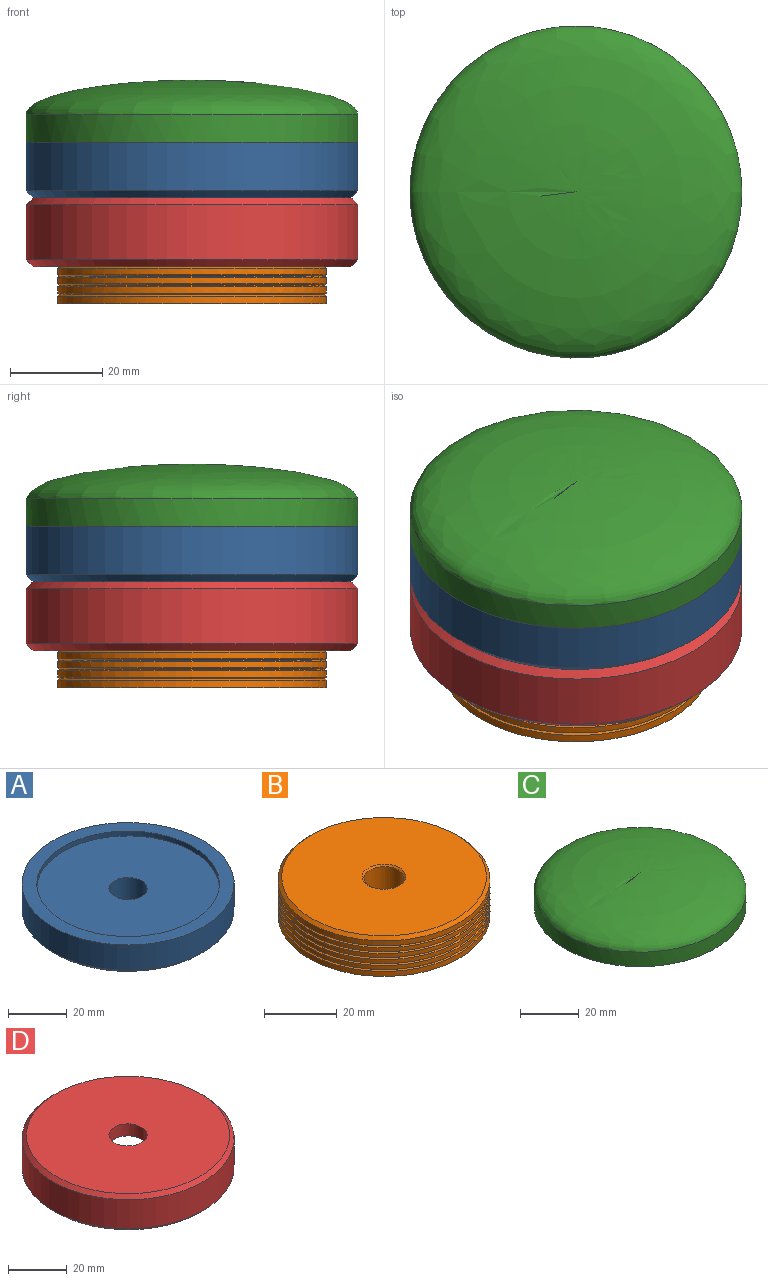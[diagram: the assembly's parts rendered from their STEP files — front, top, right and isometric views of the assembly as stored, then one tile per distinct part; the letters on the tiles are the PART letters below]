
ASSEMBLY  parts=4 mates=3
PART A: 9 faces, bbox 72x72x12 mm
  f0: plane 62x62mm, normal (0,0,1), area 2886.3mm2, adj f1,f7
  f1: cylinder r=6.5mm len=13mm, axis (0,0,-1), area 367.6mm2, adj f0,f5
  f2: cylinder r=36mm len=72mm, axis (0,0,-1), area 2375mm2, adj f6,f8
  f3: plane 69x69mm, normal (0,0,-1), area 720.2mm2, adj f4,f6
  f4: cylinder r=31mm len=62mm, axis (0,0,-1), area 194.8mm2, adj f3,f5
  f5: plane 62x62mm, normal (0,0,-1), area 2886.3mm2, adj f1,f4
  f6: cone r=36mm half-angle=45deg, axis (0,0,1), area 469.8mm2, adj f2,f3
  f7: cylinder r=31mm len=62mm, axis (0,0,-1), area 389.6mm2, adj f0,f8
  f8: plane 72x72mm, normal (0,0,1), area 1052.4mm2, adj f2,f7
PART B: 22 faces, bbox 58.3x58.3x13 mm
  f0: cylinder r=29.15mm len=58.3mm, axis (0,0,-1), area 307.4mm2, adj f2,f4
  f1: plane 56.3x56.3mm, normal (0,0,1), area 2376.4mm2, adj f2,f21
  f2: cone r=28.15mm half-angle=45deg, axis (0,0,-1), area 254.6mm2, adj f0,f1
  f3: cone r=29.75mm half-angle=54.5deg, axis (0,0,-1), area 100.7mm2, adj f4,f5
  f4: cone r=28.7mm half-angle=54.5deg, axis (0,0,1), area 100.7mm2, adj f0,f3
  f5: cylinder r=29.15mm len=58.3mm, axis (0,0,-1), area 248.4mm2, adj f3,f7
  f6: cone r=29.75mm half-angle=54.5deg, axis (0,0,-1), area 100.7mm2, adj f7,f8
  f7: cone r=28.7mm half-angle=54.5deg, axis (0,0,1), area 100.7mm2, adj f5,f6
  f8: cylinder r=29.15mm len=58.3mm, axis (0,0,-1), area 248.4mm2, adj f6,f10
  f9: cone r=29.75mm half-angle=54.5deg, axis (0,0,-1), area 100.7mm2, adj f10,f11
  f10: cone r=28.7mm half-angle=54.5deg, axis (0,0,1), area 100.7mm2, adj f8,f9
  f11: cylinder r=29.15mm len=58.3mm, axis (0,0,-1), area 248.4mm2, adj f9,f13
  f12: cone r=29.75mm half-angle=54.5deg, axis (0,0,-1), area 100.7mm2, adj f13,f14
  f13: cone r=28.7mm half-angle=54.5deg, axis (0,0,1), area 100.7mm2, adj f11,f12
  f14: cylinder r=29.15mm len=58.3mm, axis (0,0,-1), area 248.4mm2, adj f12,f16
  f15: cone r=29.75mm half-angle=54.5deg, axis (0,0,-1), area 100.7mm2, adj f16,f18
  f16: cone r=28.7mm half-angle=54.5deg, axis (0,0,1), area 100.7mm2, adj f14,f15
  f17: plane 58.3x58.3mm, normal (0,0,-1), area 2669.5mm2, adj f18
  f18: cylinder r=29.15mm len=58.3mm, axis (0,0,-1), area 307.4mm2, adj f15,f17
  f19: cylinder r=5.5mm len=11mm, axis (0,0,1), area 328.3mm2, adj f20,f21
  f20: plane 11x11mm, normal (0,0,1), area 95mm2, adj f19
  f21: cone r=5.5mm half-angle=45deg, axis (0,0,1), area 25.5mm2, adj f1,f19
PART C: 7 faces, bbox 72x72x15.5 mm
  f0: cylinder r=31mm len=62mm, axis (0,0,-1), area 389.6mm2, adj f1,f3
  f1: plane 62x62mm, normal (0,0,-1), area 2842.4mm2, adj f0,f5
  f2: cylinder r=36mm len=72mm, axis (0,0,1), area 1357.2mm2, adj f3,f4
  f3: plane 72x72mm, normal (0,0,-1), area 1052.4mm2, adj f0,f2
  f4: revolved ~72x72mm, area 4478.2mm2, adj f2
  f5: cylinder r=7.5mm len=15mm, axis (0,0,-1), area 471.2mm2, adj f1,f6
  f6: plane 15x15mm, normal (0,0,-1), area 176.7mm2, adj f5
PART D: 9 faces, bbox 72x72x15 mm
  f0: cylinder r=29.3mm len=58.6mm, axis (0,0,-1), area 1748.9mm2, adj f3,f8
  f1: cylinder r=36mm len=72mm, axis (0,0,-1), area 2714.3mm2, adj f6,f7
  f2: plane 69x69mm, normal (0,0,-1), area 949.4mm2, adj f6,f8
  f3: plane 58.6x58.6mm, normal (0,0,-1), area 2564.3mm2, adj f0,f4
  f4: cylinder r=6.5mm len=13mm, axis (0,0,-1), area 204.2mm2, adj f3,f5
  f5: plane 69x69mm, normal (0,0,1), area 3606.5mm2, adj f4,f7
  f6: cone r=36mm half-angle=45deg, axis (0,0,1), area 469.8mm2, adj f1,f2
  f7: cone r=34.5mm half-angle=45deg, axis (0,0,-1), area 469.8mm2, adj f1,f5
  f8: cone r=29.8mm half-angle=45deg, axis (0,0,-1), area 131.3mm2, adj f0,f2
PLACE A t=(32.89,34.14,39.23)mm
PLACE B t=(32.89,34.14,16.23)mm
PLACE C t=(32.89,34.14,49.23)mm
PLACE D t=(32.89,34.14,24.23)mm
MATE fastened A.f4 <-> D.f1  axis (0,0,-1) through (32.89,34.14,39.23)mm
MATE fastened D.f0 <-> B.f0  axis (0,0,-1) through (32.89,34.14,34.23)mm
MATE fastened C.f0 <-> A.f1  axis (0,0,-1) through (32.89,34.14,49.23)mm
